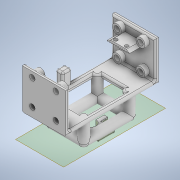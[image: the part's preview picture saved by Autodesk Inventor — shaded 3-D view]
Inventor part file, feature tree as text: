
AUTODESK INVENTOR PART (.ipt)
format: ipt  version: 2020 (Build 240168000, 168)  size: 583,168 bytes
history: native  units: in
note: dims shown in document units (in); Inventor stores cm internally (conversion verified against a paired STEP export)
features: sketch x18, extrude x16, revolve x2, fillet x2, plane x1, mirror x1
ambient origin geometry x8: Origin, YZ Plane, XZ Plane, XY Plane, X Axis, Y Axis, Z Axis, Center Point
bodies: Solid1 (feature_tree)
feature tree (40):
  extrude  "Extrusion1"  Depth=4.0157in
  extrude  "Extrusion2"  Depth=0.1575in
  extrude  "Extrusion3"  Depth=1.5748in TaperAngle=0.0deg
  extrude  "Extrusion4"  Depth=0.2362in
  extrude  "Extrusion9"  Depth=0.2362in
  extrude  "Extrusion10"  Depth=0.3937in
  extrude  "Extrusion11"  Depth=0.3937in
  revolve  "Revolution1"  [1 undecoded]
  revolve  "Revolution2"  [1 undecoded]
  extrude  "Extrusion12"  Depth=0.3937in
  plane  "Work Plane1"
  extrude  "Extrusion13"  Depth=0.3937in
  extrude  "Extrusion14"  Depth=0.3937in TaperAngle=0.0deg
  extrude  "Extrusion15"  Depth=0.3937in
  mirror  "Mirror1"
  extrude  "Extrusion16"  TaperAngle=90.0deg  [1 undecoded]
  fillet  "Fillet1"  [1 undecoded]
  extrude  "Extrusion17"  Depth=0.3937in
  fillet  "Fillet2"  Radius=1.9685in
  extrude  "Extrusion18"  Depth=1.1811in
  extrude  "Extrusion19"  Depth=0.2362in
  extrude  "Extrusion20"  Depth=0.4724in
  sketch  "Sketch1"  dims[d0=1.8898in d1=4.0157in]
  sketch  "Sketch2"  dims[d2=0.1575in d3=0.0in d4=0.1575in]
  sketch  "Sketch3"  dims[d5=0.1575in d6=1.5748in d7=0.0in]
  sketch  "Sketch4"  dims[d8=0.2362in d9=0.2362in]
  sketch  "Sketch9"  dims[d10=0.2362in d11=0.2362in]
  sketch  "Sketch10"  dims[d12=1.5748in d13=0.0in d14=0.3937in]
  sketch  "Sketch11"  dims[d15=0.3937in d16=0.3937in]
  sketch  "Sketch12"  dims[d17=0.3937in d18=0.1969in d19=0.0in]
  sketch  "Sketch13"  dims[d92=1.378in d93=1.9685in]
  sketch  "Sketch14"  dims[d94=0.6791in d95=0.0in d96=0.3937in]
  sketch  "Sketch15"  dims[d97=0.3937in d98=0.3937in]
  sketch  "Sketch16"  dims[d99=0.3937in d100=0.9449in d101=0.0in]
  sketch  "Sketch17"  dims[d102=0.3937in d103=0.3937in]
  sketch  "Sketch18"  dims[d104=1.378in d105=0.0in d106=90.0deg d107=90.0deg]
  sketch  "Sketch19"  dims[d108=0.3937in d109=0.3937in d110=1.9685in d111=0.0in]
  sketch  "Sketch20"  dims[d112=0.9843in d113=1.1811in]
  sketch  "Sketch21"  dims[d114=0.1969in d115=0.1969in d116=0.0in d117=0.0in d118=0.2362in]
  sketch  "Sketch22"  dims[d119=0.4921in d120=0.0in d121=0.4724in d122=0.5315in d123=0.2362in d124=0.5315in d125=0.2362in d126=0.2362in d127=0.0in d128=0.1575in d129=0.1575in d130=0.2362in d131=0.0in d132=0.0787in d133=0.315in d134=0.3937in d135=0.5906in d136=0.1575in d137=0.0in d138=0.0in d139=0.0787in d140=0.0591in d141=45.0deg d142=0.0591in d143=0.0591in d144=90.0deg d145=0.0591in d146=90.0deg d147=0.0591in d148=90.0deg d149=0.0591in d150=90.0deg d151=0.0591in d152=90.0deg d153=0.0591in d154=90.0deg d155=0.0591in d156=90.0deg d157=0.0591in d158=90.0deg d159=0.0591in d160=90.0deg d161=0.0591in d162=90.0deg d163=0.0591in d164=90.0deg d165=0.0591in d166=90.0deg d167=0.0591in d168=90.0deg d169=0.0591in d170=90.0deg d171=0.0591in d172=90.0deg d173=0.0591in d174=90.0deg d175=0.0591in d176=90.0deg d177=0.0591in d178=90.0deg d179=0.0591in d180=90.0deg d181=0.0591in d182=90.0deg d183=0.0591in d184=90.0deg d185=0.0591in d186=90.0deg d187=0.6299in d188=0.0in d189=0.4134in d190=0.4134in d191=0.5906in d192=0.0in d193=0.1575in d194=0.1575in d195=0.1969in d196=0.0in]
note: 4 required parameter values undecoded (feature->parameter linkage not recoverable at this tier; creation-order binding heuristic only, values carry confidence <= 0.55)